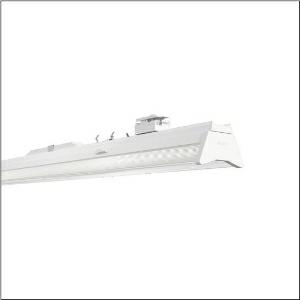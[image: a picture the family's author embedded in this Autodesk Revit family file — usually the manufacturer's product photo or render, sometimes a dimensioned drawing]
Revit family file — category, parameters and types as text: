
# Revit family: licross_21_performance_mo_52tm16cn49xg
name_source: partatom
category: Lighting Fixtures
units: mm (PartAtom-declared; Revit-internal decimal feet)

## family parameters
Cut with Voids When Loaded = No
Host = Face
Light Source = No
Part Type = Normal
Room Calculation Point = No
Round Connector Dimension = Use Diameter
Shared = No

## types (1)
- --- (1 x LED, 9240 lm, 50.4 W, 4000K)
    Apparent Load = 50 VA
    CIE Flux Codes = 66 88 96 79 100
    Color Rendering = 80
    Color Temperature = 4000K
    Default Elevation = 1800 mm
    Description = Licross 21 Performance MO, luminaire insert, of sheet steel, galvanised, coil coated, white, length: 1.500mm, width: 120mm, height: 123mm, LED rated luminous flux: 9.240lm, light colour: 840, SDCM (Standard Deviation of Colour Matching)MacAdam ≤ 3 SDCM (initial), control gear: ON/OFF Multilumen, CLOi, with plug, 3-pole, with phase selection, mains connection: 220..240V, AC, 50/60Hz, start of lifetime: 50W, end of service life: 61W, internal wiring halogen-free, primary light control with lens, of plastic, primary optical cover: cover, of PMMA, light emission: direct/indirect distribution, primary light characteristic: symmetric, protection rating (complete): IP40, insulation class (complete): insulation class I (protective earthing), certification: CE, ENEC, UKCA, protection symbol: D if used in an environment without relevant dust loads with corresponding accessories, impact resistance: IK06, permissible ambient temperature for indoor applications: -35..+45°C, corresponds to IFS (International Featured Standards) requirements for safety and quality in the food industry, reducing of maximum allowable ambient temperature of 5°C with ceiling mounting, LABS conformity tested according to VDMA 24364:2018-05, The light source and the operating device comply with the requirements of the Ecodesign Regulation (EU) 2019/2020 and are replaceable in accordance with this regulation, packaging unit: 1 piece
    Height = 114 mm
    Lamp = 1 x LED
    Lamp Light Flux = 9240 lm
    Lamp Power = 50.4 W
    Lamp count = 1
    Length = 1500 mm
    Luminous efficacy = 183 lm/W
    Manufacturer = Siteco
    ModVariant = No
    Model = 52TM16CN49XG
    Mounting Place = Ceiling
    Mounting Type = Pendant
    Number of Poles = 1
    OnlyDefault = Yes
    Power Factor = 1
    Product Name = Licross 21 Performance MO
    Product group = luminaire insert | ceiling pendant
    ProductGroupID = 901
    Protection Class = Protection class I
    Protection Degree = IP 40
    RLX_Detail_Level = 1
    RLX_Emergency_Light_Flux = 0 lm
    RLX_Emergency_Type = 0
    RLX_Emergency_Type_DB = No
    RlxData = <blob elided: 32117 chars, md5=1f5031fa>
    Socket = socket
    Standby Power = 0 W
    System Light Flux = 9240 lm
    System Power = 50 W
    Type Comments = factory setting: luminous flux: 100 % | (A | C | E) | 117 mA
    Type Image = l_1256138.jpg
    URL = http://relux.com
    VarID = @adj_111545
    Voltage = 0 V
    Weight = 0.00 kg
    Width = 120 mm

## geometry (parser evidence)
native form markers: Blend x4, Sweep x13
no freeform markers — native parametric forms only
